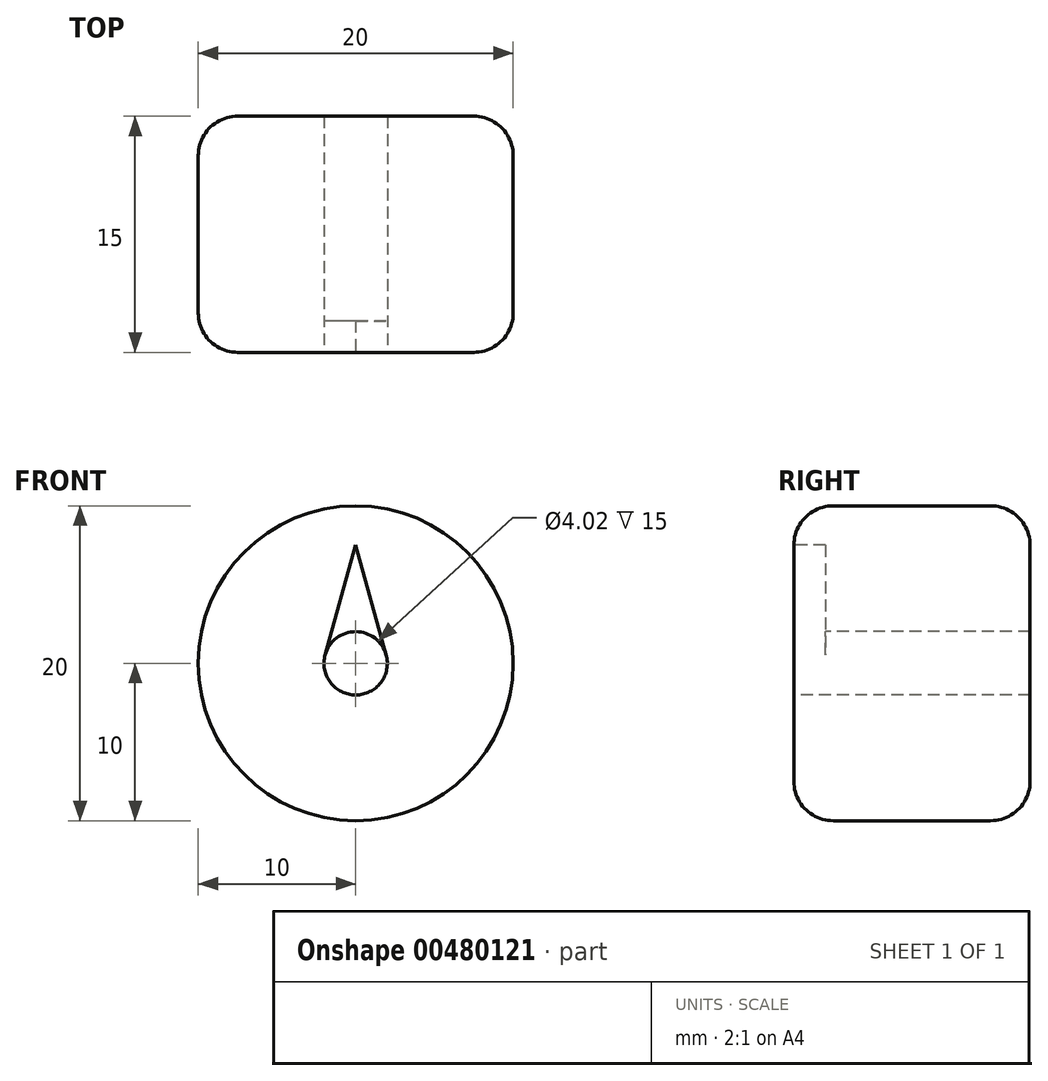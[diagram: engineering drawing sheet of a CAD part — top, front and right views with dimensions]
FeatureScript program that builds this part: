
annotation { "Feature Type Name" : "Feature", "Feature Type Description" : "" }
export const myFeature = defineFeature(function(context is Context, id is Id, definition is map)
    precondition{}
    {
        {
            var Q0;
            Q0=qCreatedBy(makeId("Front.planeOp"),FACE);
            var sketch = newSketch(context, id + "F0", { "sketchPlane" : qUnion([Q0])});
            skCircle(sketch, "E0", {"center": v(0, 0) * mm, "radius": 10 * mm});
            skCircle(sketch, "E1", {"center": v(0, 0) * mm, "radius": 9 * mm});
            skSolve(sketch);
        }
        {
            var Q0;
            Q0=makeQuery(id+"F0.imprint","IMPRINT",FACE,{"disambiguationData":[TD([[makeQuery(id+"F0.imprint","IMPRINT",EDGE,{"derivedFrom":sQuery(id+"F0.wireOp",EDGE,"E0")}),1.0]])]});
            var Q1;
            Q1=makeQuery(id+"F0.imprint","IMPRINT",FACE,{"disambiguationData":[TD([[makeQuery(id+"F0.imprint","IMPRINT",EDGE,{"derivedFrom":sQuery(id+"F0.wireOp",EDGE,"E1")}),1.0]])]});
            extrude(context, id + "F1", {"entities" : qUnion([Q0, Q1]), "depth" : 15 * mm});
        }
        {
            var Q0;
            Q0=makeQuery(id+"F1.opExtrude","CAP_EDGE",EDGE,{"disambiguationData":[OSD([sQuery(id+"F0.wireOp",EDGE,"E0")])],"isStart":false});
            var Q1;
            Q1=makeQuery(id+"F1.opExtrude","CAP_EDGE",EDGE,{"disambiguationData":[OSD([sQuery(id+"F0.wireOp",EDGE,"E0")])],"isStart":true});
            fillet(context, id + "F2", {"entities" : qUnion([Q0, Q1]), "radius" : 2.5 * mm, "tangentPropagation" : true, "allowEdgeOverflow" : false});
        }
        {
            var Q0;
            Q0=makeQuery(id+"F1.opExtrude","CAP_FACE",FACE,{"disambiguationData":[OSD([sQuery(id+"F0.wireOp",EDGE,"E0")])],"isStart":false});
            var sketch = newSketch(context, id + "F3", { "sketchPlane" : qUnion([Q0])});
            skCircle(sketch, "E2", {"center": v(0, 0) * mm, "radius": 2.01 * mm});
            skLineSegment(sketch, "E3", {"start": v(0, 7.5) * mm, "end": v(-1.94, 0.54) * mm});
            skLineSegment(sketch, "E4", {"start": v(0, 7.5) * mm, "end": v(1.94, 0.54) * mm});
            skSolve(sketch);
        }
        {
            var Q0;
            {var subQ0=sQuery(id+"F3.wireOp",EDGE,"E2");var subQ1=makeQuery(id+"F3.imprint","INTERSECT",VERTEX,{"derivedFrom":[subQ0,sQuery(id+"F3.wireOp",EDGE,"E3")]});Q0=makeQuery(id+"F3.imprint","IMPRINT",FACE,{"disambiguationData":[TD([[makeQuery(id+"F3.imprint","IMPRINT",EDGE,{"disambiguationData":[TD([[subQ1,1.0]])],"derivedFrom":subQ0}),1.0]])]});}
            extrude(context, id + "F4", {"entities" : qUnion([Q0]), "operationType" : NewBodyOperationType.REMOVE, "oppositeDirection" : true, "depth" : 50 * mm});
        }
        {
            var Q0;
            {var subQ0=sQuery(id+"F3.wireOp",EDGE,"E3");Q0=makeQuery(id+"F3.imprint","IMPRINT",FACE,{"disambiguationData":[TD([[makeQuery(id+"F3.imprint","IMPRINT",EDGE,{"derivedFrom":subQ0}),1.0]])]});}
            extrude(context, id + "F5", {"entities" : qUnion([Q0]), "operationType" : NewBodyOperationType.REMOVE, "oppositeDirection" : true, "depth" : 2 * mm});
        }
    });
